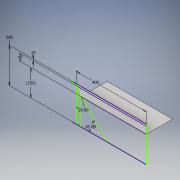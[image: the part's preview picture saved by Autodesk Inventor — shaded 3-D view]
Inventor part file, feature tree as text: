
AUTODESK INVENTOR PART (.ipt)
format: ipt  version: 2019 (Build 230136000, 136)  size: 150,016 bytes
history: native  units: mm
features: sheet_metal_op x3, sketch x2, other x1
ambient origin geometry x8: Origin, YZ Plane, XZ Plane, XY Plane, X Axis, Y Axis, Z Axis, Center Point
bodies: Solid1 (feature_tree)
feature tree (6):
  sketch  "Sketch1"  dims[d0=200.0mm]
  sheet_metal_op  "Face1"
  sheet_metal_op  "Fold2"
  sheet_metal_op  "Hem1"
  other  "Plate1"
  sketch  "Sketch2"  dims[d2=10.0mm d3=40.0mm d4=150.0mm d5=45.0deg d7=45.0deg d8=10.0mm d9=40.0mm d10=400.0mm d12=4.886922mm d13=0.5mm d20=0.5mm d21=0.25mm d22=1.0mm d23=0.5mm d24=90.0deg d25=0.5mm d26=0.5mm d27=0.25mm d28=1.0mm d29=0.5mm d30=10.0mm d31=0.25mm d32=0.125mm]
